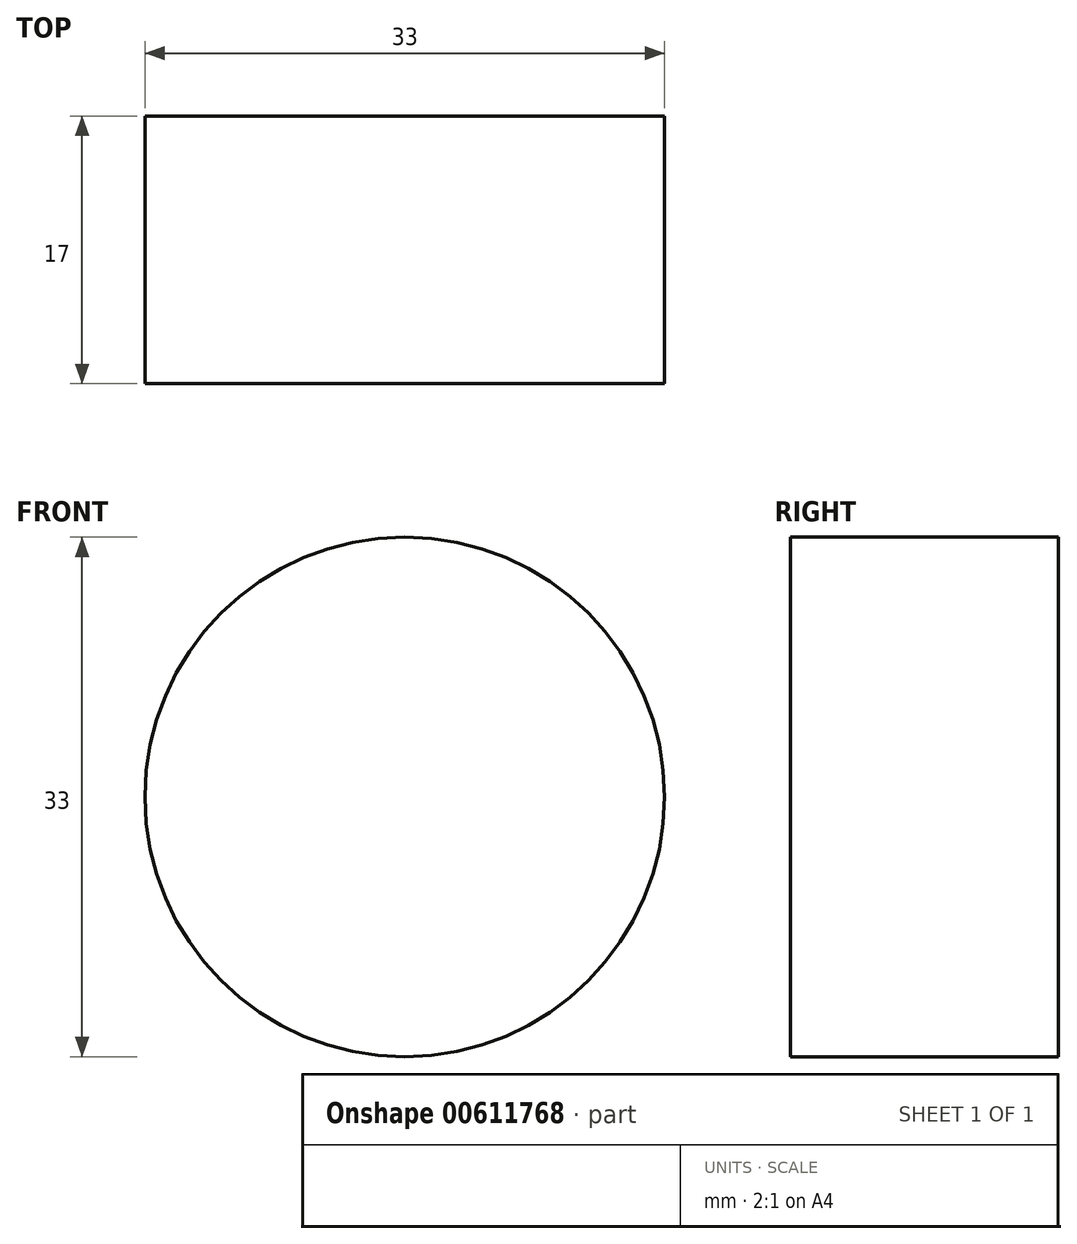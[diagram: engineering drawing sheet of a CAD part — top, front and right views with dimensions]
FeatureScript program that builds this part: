
annotation { "Feature Type Name" : "Feature", "Feature Type Description" : "" }
export const myFeature = defineFeature(function(context is Context, id is Id, definition is map)
    precondition{}
    {
        {
            var Q0;
            Q0=qCreatedBy(makeId("Right.planeOp"),FACE);
            var sketch = newSketch(context, id + "F0", { "sketchPlane" : qUnion([Q0])});
            skLineSegment(sketch, "E0", {"start": v(0, 0) * mm, "end": v(0, 16.5) * mm});
            skLineSegment(sketch, "E1", {"start": v(0, 16.5) * mm, "end": v(17, 16.5) * mm});
            skLineSegment(sketch, "E2", {"start": v(17, 16.5) * mm, "end": v(17, 0) * mm});
            skLineSegment(sketch, "E3", {"start": v(17, 0) * mm, "end": v(0, 0) * mm});
            skLineSegment(sketch, "E4", {"start": v(0, 1.5) * mm, "end": v(10.02, 1.5) * mm});
            skPoint(sketch, "E5.end.orphan", {"position": v(0, 6.26) * mm});
            skPoint(sketch, "E6.start.orphan", {"position": v(0, 4.87) * mm});
            skLineSegment(sketch, "E7", {"start": v(10.02, 1.5) * mm, "end": v(10.02, 5.99) * mm});
            skLineSegment(sketch, "E8", {"start": v(10.02, 5.99) * mm, "end": v(7.3, 5.99) * mm});
            skLineSegment(sketch, "E9", {"start": v(7.3, 5.99) * mm, "end": v(7.3, 3.74) * mm});
            skLineSegment(sketch, "E10", {"start": v(7.3, 3.74) * mm, "end": v(0, 3.74) * mm});
            skLineSegment(sketch, "E11", {"start": v(0, 3.74) * mm, "end": v(0, 1.5) * mm});
            skSolve(sketch);
        }
        {
            var Q0;
            Q0=makeQuery(id+"F0.imprint","IMPRINT",FACE,{"disambiguationData":[TD([[makeQuery(id+"F0.imprint","IMPRINT",EDGE,{"derivedFrom":sQuery(id+"F0.wireOp",EDGE,"E4")}),1.0]])]});
            var Q1;
            {var subQ0=sQuery(id+"F0.wireOp",EDGE,"E1");Q1=makeQuery(id+"F0.imprint","IMPRINT",FACE,{"disambiguationData":[TD([[makeQuery(id+"F0.imprint","IMPRINT",EDGE,{"derivedFrom":subQ0}),-1.0]])]});}
            var Q2;
            Q2=sQuery(id+"F0.wireOp",EDGE,"E3");
            revolve(context, id + "F1", {"entities" : qUnion([Q0, Q1]), "axis" : qUnion([Q2]), "revolveType" : RevolveType.FULL});
        }
    });
